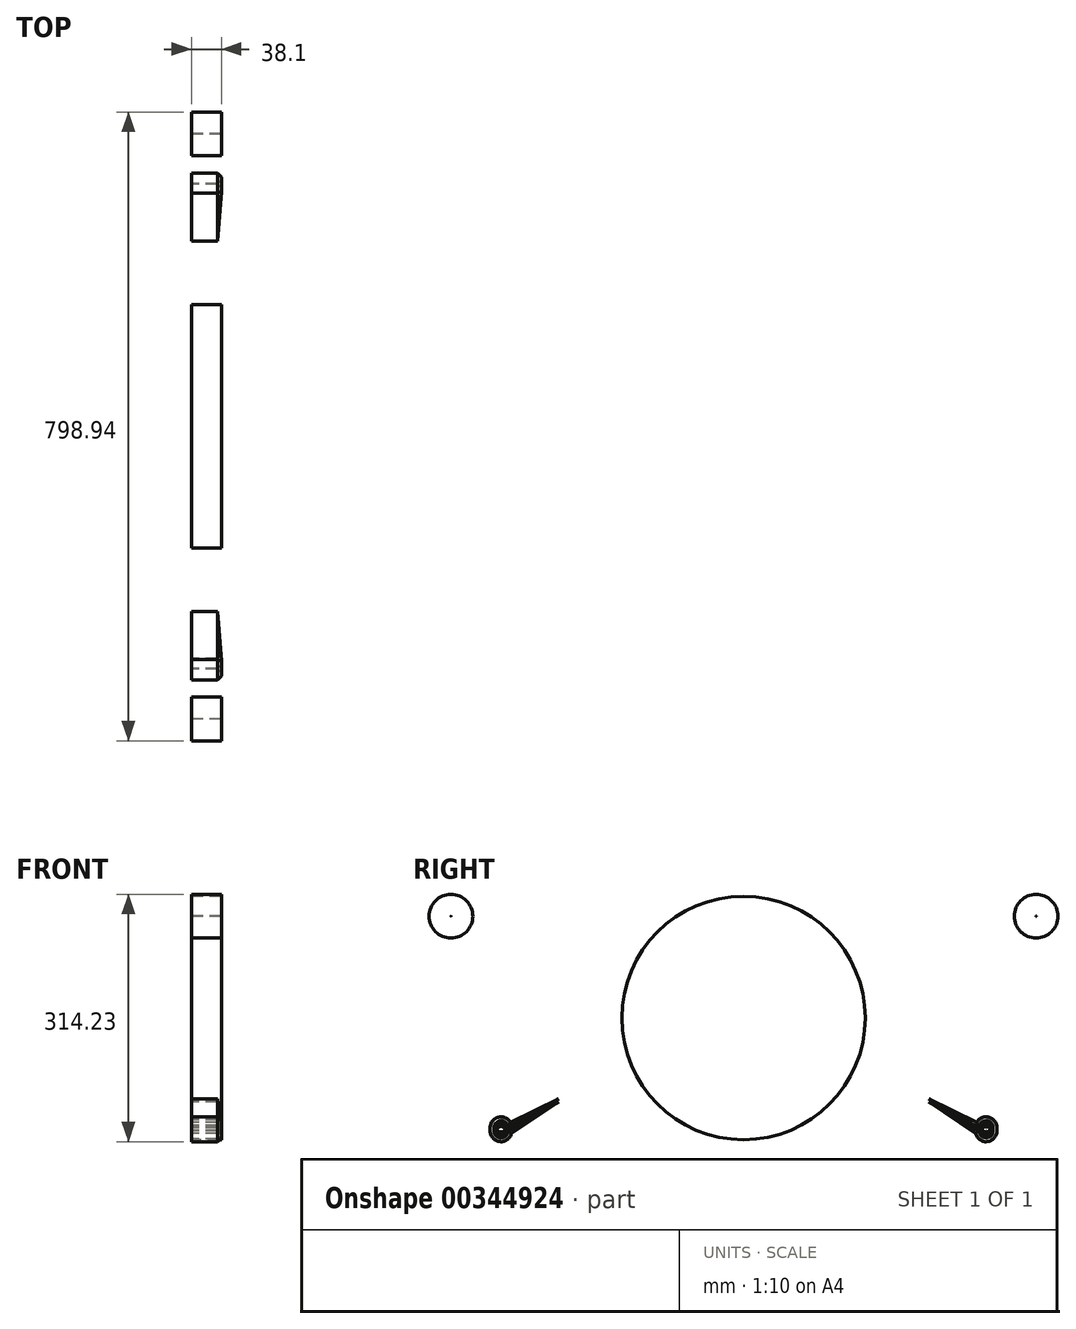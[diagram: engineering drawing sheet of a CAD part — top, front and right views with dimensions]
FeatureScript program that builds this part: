
annotation { "Feature Type Name" : "Feature", "Feature Type Description" : "" }
export const myFeature = defineFeature(function(context is Context, id is Id, definition is map)
    precondition{}
    {
        {
            var Q0;
            Q0=qCreatedBy(makeId("Right.planeOp"),FACE);
            var sketch = newSketch(context, id + "F0", { "sketchPlane" : qUnion([Q0])});
            skCircle(sketch, "E0", {"center": v(0, 0) * mm, "radius": 154.57 * mm});
            skCircle(sketch, "E1", {"center": v(371.64, 129.37) * mm, "radius": 27.83 * mm});
            skCircle(sketch, "E2", {"center": v(371.64, 129.37) * mm, "radius": 0.13 * mm});
            skCircle(sketch, "E3", {"center": v(308.13, -139.38) * mm, "radius": 13.85 * mm});
            skCircle(sketch, "E4", {"center": v(308.13, -139.38) * mm, "radius": 0.27 * mm});
            skLineSegment(sketch, "E5", {"start": v(347.8, 115.03) * mm, "end": v(302.65, -126.66) * mm});
            skLineSegment(sketch, "E6", {"start": v(348.52, 144.87) * mm, "end": v(296.96, -131.2) * mm});
            skLineSegment(sketch, "E7", {"start": v(296.12, -132.49) * mm, "end": v(143.3, -57.98) * mm});
            skLineSegment(sketch, "E8", {"start": v(294.75, -142.94) * mm, "end": v(148.15, -44.1) * mm});
            skLineSegment(sketch, "E9", {"start": v(343.85, 127.78) * mm, "end": v(130.86, 82.27) * mm});
            skLineSegment(sketch, "E10", {"start": v(355.89, 152.32) * mm, "end": v(88.33, 126.85) * mm});
            skLineSegment(sketch, "E11.MirrorCS", {"start": v(-355.89, 152.32) * mm, "end": v(-88.33, 126.85) * mm});
            skLineSegment(sketch, "E12.MirrorCS", {"start": v(-343.85, 127.78) * mm, "end": v(-130.86, 82.27) * mm});
            skLineSegment(sketch, "E13.MirrorCS", {"start": v(-348.52, 144.87) * mm, "end": v(-296.96, -131.2) * mm});
            skLineSegment(sketch, "E14.MirrorCS", {"start": v(-347.8, 115.03) * mm, "end": v(-302.65, -126.66) * mm});
            skCircle(sketch, "E15.MirrorC", {"center": v(-371.64, 129.37) * mm, "radius": 27.83 * mm});
            skCircle(sketch, "E16.MirrorC", {"center": v(-371.64, 129.37) * mm, "radius": 0.13 * mm});
            skCircle(sketch, "E17.MirrorC", {"center": v(-308.13, -139.38) * mm, "radius": 13.85 * mm});
            skCircle(sketch, "E18.MirrorC", {"center": v(-308.13, -139.38) * mm, "radius": 0.27 * mm});
            skLineSegment(sketch, "E19.MirrorCS", {"start": v(-294.75, -142.94) * mm, "end": v(-148.15, -44.1) * mm});
            skLineSegment(sketch, "E20.MirrorCS", {"start": v(-296.12, -132.49) * mm, "end": v(-143.3, -57.98) * mm});
            skSolve(sketch);
        }
        {
            var Q0;
            Q0=qSketchRegion(id+"F0",true);
            extrude(context, id + "F1", {"entities" : qUnion([Q0]), "depth" : 25.4 * mm});
        }
        {
            var Q0;
            Q0=qSketchRegion(id+"F0",true);
            extrude(context, id + "F2", {"entities" : qUnion([Q0]), "operationType" : NewBodyOperationType.ADD, "endBound" : BoundingType.SYMMETRIC, "depth" : 12.7 * mm});
        }
        {
            var Q0;
            Q0=makeQuery(id+"F2.opExtrude","CAP_FACE",FACE,{"disambiguationData":[OSD([sQuery(id+"F0.wireOp",EDGE,"E0"),sQuery(id+"F0.wireOp",EDGE,"E1"),sQuery(id+"F0.wireOp",EDGE,"E2"),sQuery(id+"F0.wireOp",EDGE,"E3"),sQuery(id+"F0.wireOp",EDGE,"E4"),sQuery(id+"F0.wireOp",EDGE,"E5"),sQuery(id+"F0.wireOp",EDGE,"E6"),sQuery(id+"F0.wireOp",EDGE,"E7"),sQuery(id+"F0.wireOp",EDGE,"E8"),sQuery(id+"F0.wireOp",EDGE,"E9"),sQuery(id+"F0.wireOp",EDGE,"E10"),sQuery(id+"F0.wireOp",EDGE,"E11.MirrorCS"),sQuery(id+"F0.wireOp",EDGE,"E12.MirrorCS"),sQuery(id+"F0.wireOp",EDGE,"E13.MirrorCS"),sQuery(id+"F0.wireOp",EDGE,"E14.MirrorCS"),sQuery(id+"F0.wireOp",EDGE,"E15.MirrorC"),sQuery(id+"F0.wireOp",EDGE,"E16.MirrorC"),sQuery(id+"F0.wireOp",EDGE,"E17.MirrorC"),sQuery(id+"F0.wireOp",EDGE,"E18.MirrorC"),sQuery(id+"F0.wireOp",EDGE,"E19.MirrorCS"),sQuery(id+"F0.wireOp",EDGE,"E20.MirrorCS")])],"isStart":true});
            chamfer(context, id + "F3", {"entities" : qUnion([Q0]), "width" : 5.08 * mm, "tangentPropagation" : true});
        }
        {
            var Q0;
            Q0=makeQuery(id+"F1.opExtrude","CAP_FACE",FACE,{"disambiguationData":[OSD([sQuery(id+"F0.wireOp",EDGE,"E0"),sQuery(id+"F0.wireOp",EDGE,"E1"),sQuery(id+"F0.wireOp",EDGE,"E2"),sQuery(id+"F0.wireOp",EDGE,"E3"),sQuery(id+"F0.wireOp",EDGE,"E4"),sQuery(id+"F0.wireOp",EDGE,"E5"),sQuery(id+"F0.wireOp",EDGE,"E6"),sQuery(id+"F0.wireOp",EDGE,"E7"),sQuery(id+"F0.wireOp",EDGE,"E8"),sQuery(id+"F0.wireOp",EDGE,"E9"),sQuery(id+"F0.wireOp",EDGE,"E10"),sQuery(id+"F0.wireOp",EDGE,"E11.MirrorCS"),sQuery(id+"F0.wireOp",EDGE,"E12.MirrorCS"),sQuery(id+"F0.wireOp",EDGE,"E13.MirrorCS"),sQuery(id+"F0.wireOp",EDGE,"E14.MirrorCS"),sQuery(id+"F0.wireOp",EDGE,"E15.MirrorC"),sQuery(id+"F0.wireOp",EDGE,"E16.MirrorC"),sQuery(id+"F0.wireOp",EDGE,"E17.MirrorC"),sQuery(id+"F0.wireOp",EDGE,"E18.MirrorC"),sQuery(id+"F0.wireOp",EDGE,"E19.MirrorCS"),sQuery(id+"F0.wireOp",EDGE,"E20.MirrorCS")])],"isStart":false});
            chamfer(context, id + "F4", {"entities" : qUnion([Q0]), "width" : 5.08 * mm, "tangentPropagation" : true});
        }
        {
            var Q0;
            Q0=qSketchRegion(id+"F0",true);
            extrude(context, id + "F5", {"entities" : qUnion([Q0]), "operationType" : NewBodyOperationType.ADD, "endBound" : BoundingType.SYMMETRIC, "depth" : 25.4 * mm});
        }
        {
            var Q0;
            Q0=makeQuery(id+"F1.opExtrude","SWEPT_BODY",BODY,{"disambiguationData":[OSD([sQuery(id+"F0.wireOp",EDGE,"E0"),sQuery(id+"F0.wireOp",EDGE,"E1"),sQuery(id+"F0.wireOp",EDGE,"E2"),sQuery(id+"F0.wireOp",EDGE,"E3"),sQuery(id+"F0.wireOp",EDGE,"E4"),sQuery(id+"F0.wireOp",EDGE,"E5"),sQuery(id+"F0.wireOp",EDGE,"E6"),sQuery(id+"F0.wireOp",EDGE,"E7"),sQuery(id+"F0.wireOp",EDGE,"E8"),sQuery(id+"F0.wireOp",EDGE,"E9"),sQuery(id+"F0.wireOp",EDGE,"E10"),sQuery(id+"F0.wireOp",EDGE,"E11.MirrorCS"),sQuery(id+"F0.wireOp",EDGE,"E12.MirrorCS"),sQuery(id+"F0.wireOp",EDGE,"E13.MirrorCS"),sQuery(id+"F0.wireOp",EDGE,"E14.MirrorCS"),sQuery(id+"F0.wireOp",EDGE,"E15.MirrorC"),sQuery(id+"F0.wireOp",EDGE,"E16.MirrorC"),sQuery(id+"F0.wireOp",EDGE,"E17.MirrorC"),sQuery(id+"F0.wireOp",EDGE,"E18.MirrorC"),sQuery(id+"F0.wireOp",EDGE,"E19.MirrorCS"),sQuery(id+"F0.wireOp",EDGE,"E20.MirrorCS")])]});
            transform(context, id + "F6", {"entities" : qUnion([Q0]), "transformType" : TransformType.TRANSLATION_3D, "dx" : 0 * mm, "dy" : 0 * mm, "dz" : -3.8 * mm, "makeCopy" : true});
        }
    });
